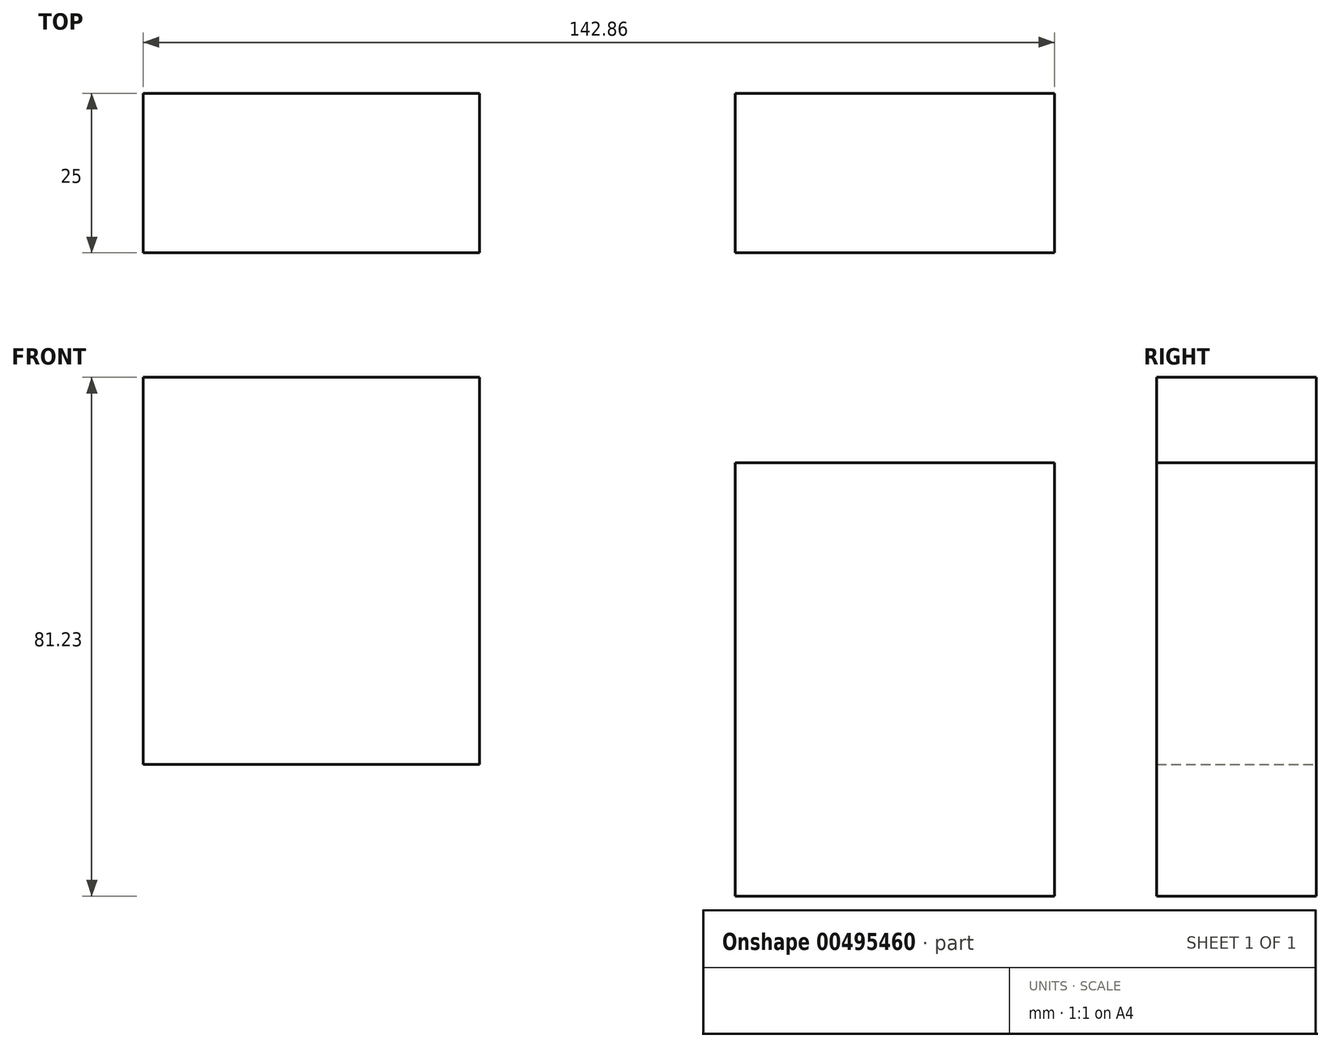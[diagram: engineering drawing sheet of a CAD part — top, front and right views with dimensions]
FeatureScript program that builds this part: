
annotation { "Feature Type Name" : "Feature", "Feature Type Description" : "" }
export const myFeature = defineFeature(function(context is Context, id is Id, definition is map)
    precondition{}
    {
        {
            var Q0;
            Q0=qCreatedBy(makeId("Front.planeOp"),FACE);
            var sketch = newSketch(context, id + "F0", { "sketchPlane" : qUnion([Q0])});
            skLineSegment(sketch, "E0.bottom", {"start": v(-120.83, -6.5) * mm, "end": v(-68.1, -6.5) * mm});
            skLineSegment(sketch, "E0.top", {"start": v(-120.83, 54.11) * mm, "end": v(-68.1, 54.11) * mm});
            skLineSegment(sketch, "E0.left", {"start": v(-120.83, -6.5) * mm, "end": v(-120.83, 54.11) * mm});
            skLineSegment(sketch, "E0.right", {"start": v(-68.1, -6.5) * mm, "end": v(-68.1, 54.11) * mm});
            skPoint(sketch, "E0.middle", {"position": v(-94.46, 23.8) * mm});
            skLineSegment(sketch, "E1.bottom", {"start": v(-28.04, -27.12) * mm, "end": v(22.03, -27.12) * mm});
            skLineSegment(sketch, "E1.top", {"start": v(-28.04, 40.74) * mm, "end": v(22.03, 40.74) * mm});
            skLineSegment(sketch, "E1.left", {"start": v(-28.04, -27.12) * mm, "end": v(-28.04, 40.74) * mm});
            skLineSegment(sketch, "E1.right", {"start": v(22.03, -27.12) * mm, "end": v(22.03, 40.74) * mm});
            skPoint(sketch, "E1.middle", {"position": v(-3, 6.8) * mm});
            skSolve(sketch);
        }
        {
            var Q0;
            Q0 = qSketchRegion(id + "F0", true);
            extrude(context, id + "F1", {"entities" : qUnion([Q0]), "depth" : 25 * mm});
        }
    });
